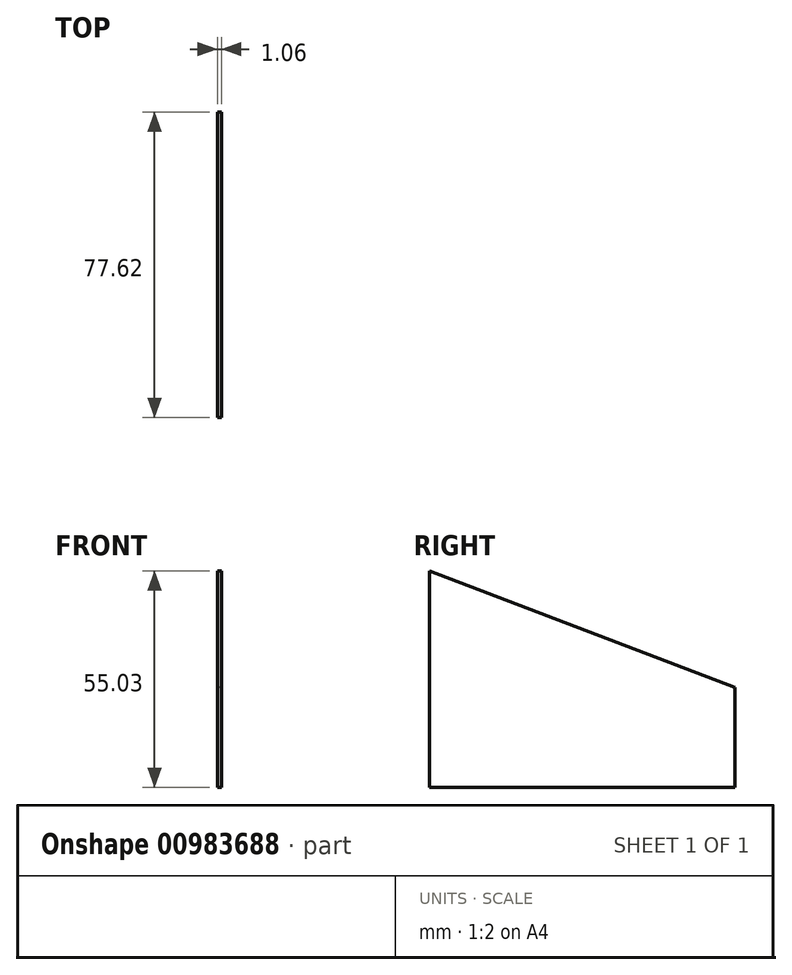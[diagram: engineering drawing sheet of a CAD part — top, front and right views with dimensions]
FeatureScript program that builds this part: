
annotation { "Feature Type Name" : "Feature", "Feature Type Description" : "" }
export const myFeature = defineFeature(function(context is Context, id is Id, definition is map)
    precondition{}
    {
        {
            var Q0;
            Q0=qCreatedBy(makeId("Right.planeOp"),FACE);
            var sketch = newSketch(context, id + "F0", { "sketchPlane" : qUnion([Q0])});
            skLineSegment(sketch, "E0.top", {"start": v(38.81, -12.7) * mm, "end": v(-38.81, -12.7) * mm});
            skLineSegment(sketch, "E0.left", {"start": v(38.81, 12.7) * mm, "end": v(38.81, -12.7) * mm});
            skLineSegment(sketch, "E0.right", {"start": v(-38.81, 12.7) * mm, "end": v(-38.81, -12.7) * mm});
            skPoint(sketch, "E0.middle", {"position": v(0, 0) * mm});
            skLineSegment(sketch, "E1", {"start": v(-38.81, 12.7) * mm, "end": v(-38.81, 42.33) * mm});
            skLineSegment(sketch, "E2", {"start": v(-38.81, 42.33) * mm, "end": v(38.81, 12.7) * mm});
            skSolve(sketch);
        }
        {
            var Q0;
            Q0 = qSketchRegion(id + "F0", true);
            extrude(context, id + "F1", {"entities" : qUnion([Q0]), "depth" : 1.06 * mm, "offsetDistance" : 25.4 * mm});
        }
    });
